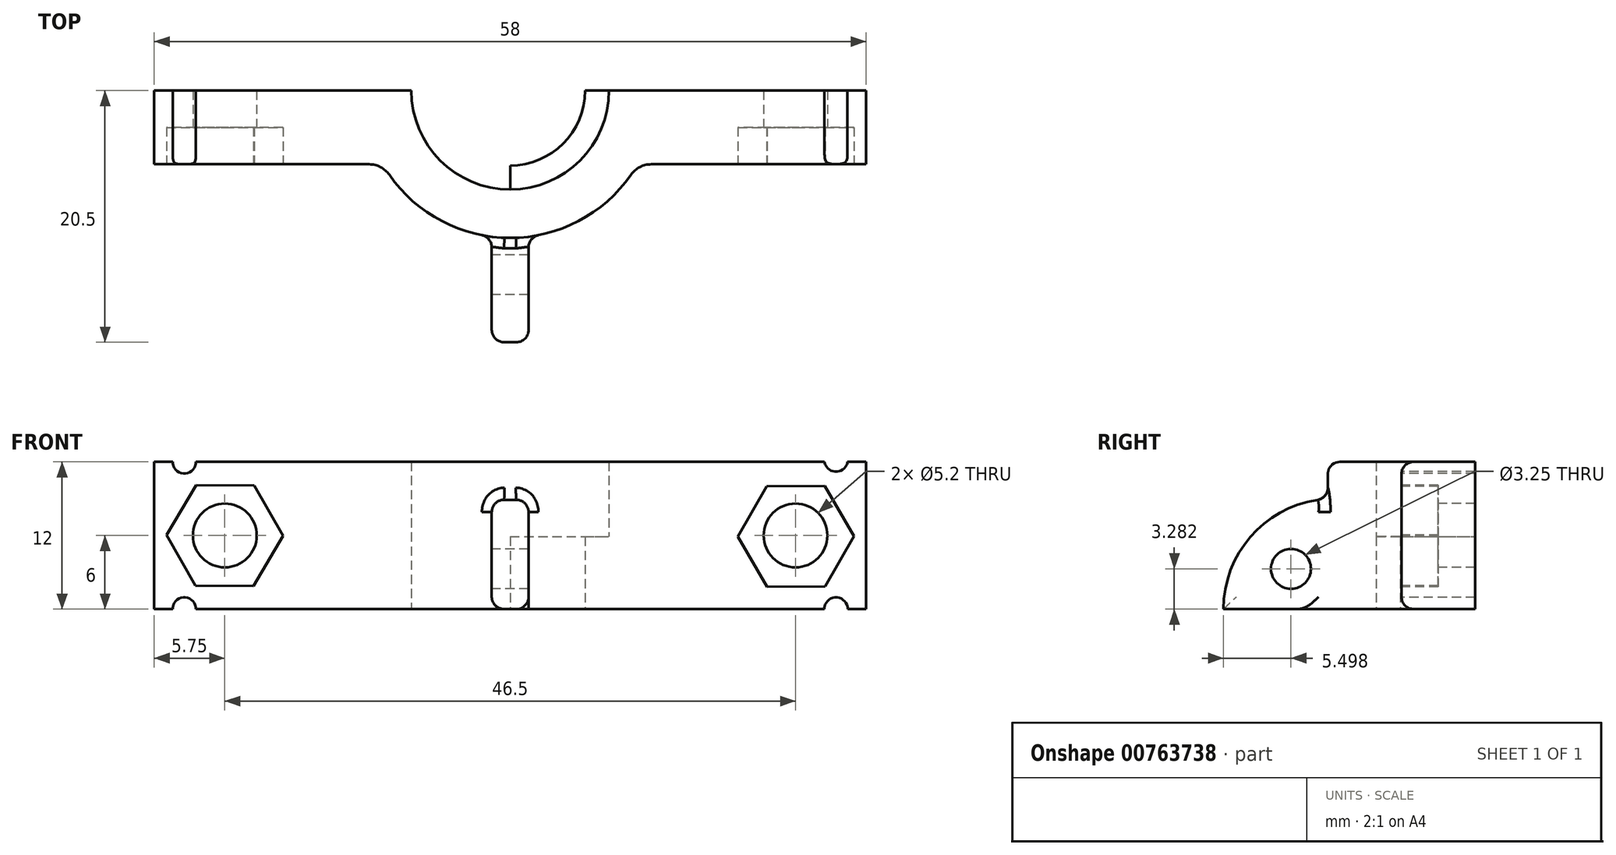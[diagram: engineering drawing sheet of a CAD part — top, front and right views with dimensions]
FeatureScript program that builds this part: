
annotation { "Feature Type Name" : "Feature", "Feature Type Description" : "" }
export const myFeature = defineFeature(function(context is Context, id is Id, definition is map)
    precondition{}
    {
        {
            var Q0;
            Q0=qCreatedBy(makeId("Top.planeOp"),FACE);
            var sketch = newSketch(context, id + "F0", { "sketchPlane" : qUnion([Q0])});
            skLineSegment(sketch, "E0", {"start": v(0, 28.15) * mm, "end": v(0, 0) * mm, "construction": true});
            skLineSegment(sketch, "E1.bottom", {"start": v(6.1, 0) * mm, "end": v(29, 0) * mm});
            skLineSegment(sketch, "E1.left", {"start": v(0, -6.1) * mm, "end": v(0, -12) * mm});
            skLineSegment(sketch, "E1.right", {"start": v(29, 0) * mm, "end": v(29, -6) * mm});
            skArc(sketch, "E2", {"start": v(0, -6.1) * mm, "mid": v(4.31, -4.31) * mm, "end": v(6.1, 0) * mm});
            skArc(sketch, "E3", {"start": v(0, -8.05) * mm, "mid": v(5.7, -5.7) * mm, "end": v(8.05, 0) * mm});
            skArc(sketch, "E4", {"start": v(0, -12) * mm, "mid": v(6, -10.4) * mm, "end": v(10.4, -6) * mm});
            skLineSegment(sketch, "E5", {"start": v(29, -6) * mm, "end": v(0, -6) * mm, "construction": true});
            skLineSegment(sketch, "E6", {"start": v(10.4, -6) * mm, "end": v(29, -6) * mm});
            skPoint(sketch, "E1.top.end.orphan", {"position": v(29, -12) * mm});
            skLineSegment(sketch, "E7", {"start": v(0, -12) * mm, "end": v(23.1, -12) * mm, "construction": true});
            skLineSegment(sketch, "E8.trimOffspring", {"start": v(0, -6.1) * mm, "end": v(0, -22.79) * mm, "construction": true});
            skLineSegment(sketch, "E9", {"start": v(0, 0) * mm, "end": v(0, -6.1) * mm, "construction": true});
            skLineSegment(sketch, "E10.MirrorCS", {"start": v(-10.4, -6) * mm, "end": v(-29, -6) * mm});
            skArc(sketch, "E11.MirrorCS", {"start": v(0, -6.1) * mm, "mid": v(-4.31, -4.31) * mm, "end": v(-6.1, 0) * mm});
            skArc(sketch, "E12.MirrorCS", {"start": v(0, -8.05) * mm, "mid": v(-5.7, -5.7) * mm, "end": v(-8.05, 0) * mm});
            skArc(sketch, "E13.MirrorCS", {"start": v(0, -12) * mm, "mid": v(-6, -10.4) * mm, "end": v(-10.4, -6) * mm});
            skLineSegment(sketch, "E14.MirrorCS", {"start": v(-29, -6) * mm, "end": v(0, -6) * mm, "construction": true});
            skLineSegment(sketch, "E15.MirrorCS", {"start": v(-6.1, 0) * mm, "end": v(-29, 0) * mm});
            skLineSegment(sketch, "E16.MirrorCS", {"start": v(-29, 0) * mm, "end": v(-29, -6) * mm});
            skPoint(sketch, "E17.orphan", {"position": v(-12, 0) * mm});
            skPoint(sketch, "E18.orphan", {"position": v(12, 0) * mm});
            skSolve(sketch);
        }
        {
            var Q0;
            Q0=makeQuery(id+"F0.imprint","IMPRINT",FACE,{"disambiguationData":[TD([[makeQuery(id+"F0.imprint","IMPRINT",EDGE,{"derivedFrom":sQuery(id+"F0.wireOp",EDGE,"E10.MirrorCS")}),-1.0]])]});
            var Q1;
            {var subQ0=sQuery(id+"F0.wireOp",EDGE,"E1.right");Q1=makeQuery(id+"F0.imprint","IMPRINT",FACE,{"disambiguationData":[TD([[makeQuery(id+"F0.imprint","IMPRINT",EDGE,{"derivedFrom":subQ0}),-1.0]])]});}
            extrude(context, id + "F1", {"entities" : qUnion([Q0, Q1]), "depth" : 12 * mm, "offsetDistance" : 25 * mm});
        }
        {
            var Q0;
            {var subQ0=sQuery(id+"F0.wireOp",EDGE,"E11.MirrorCS");Q0=makeQuery(id+"F0.imprint","IMPRINT",FACE,{"disambiguationData":[TD([[makeQuery(id+"F0.imprint","IMPRINT",EDGE,{"derivedFrom":subQ0}),1.0]])]});}
            var Q1;
            {var subQ0=sQuery(id+"F0.wireOp",EDGE,"E2");Q1=makeQuery(id+"F0.imprint","IMPRINT",FACE,{"disambiguationData":[TD([[makeQuery(id+"F0.imprint","IMPRINT",EDGE,{"derivedFrom":subQ0}),-1.0]])]});}
            extrude(context, id + "F2", {"entities" : qUnion([Q0, Q1]), "operationType" : NewBodyOperationType.ADD, "depth" : 5.9 * mm, "offsetDistance" : 25 * mm});
        }
        {
            var Q0;
            Q0=makeQuery(id+"F1.opExtrude","SWEPT_FACE",FACE,{"disambiguationData":[OSD([sQuery(id+"F0.wireOp",EDGE,"E10.MirrorCS")])]});
            var sketch = newSketch(context, id + "F3", { "sketchPlane" : qUnion([Q0])});
            skLineSegment(sketch, "E19", {"start": v(-29, 6) * mm, "end": v(33.2, 6) * mm, "construction": true});
            skLineSegment(sketch, "E20", {"start": v(29.12, 12) * mm, "end": v(37.37, 12) * mm, "construction": true});
            skLineSegment(sketch, "E21", {"start": v(29.05, 0) * mm, "end": v(37.37, 0) * mm, "construction": true});
            skCircle(sketch, "E22", {"center": v(-23.25, 6) * mm, "radius": 2.6 * mm});
            skCircle(sketch, "E23", {"center": v(23.25, 6) * mm, "radius": 2.6 * mm});
            skSolve(sketch);
        }
        {
            var Q0;
            Q0=makeQuery(id+"F3.imprint","IMPRINT",FACE,{"disambiguationData":[TD([[makeQuery(id+"F3.imprint","IMPRINT",EDGE,{"derivedFrom":sQuery(id+"F3.wireOp",EDGE,"E23")}),1.0]])]});
            var Q1;
            Q1=makeQuery(id+"F3.imprint","IMPRINT",FACE,{"disambiguationData":[TD([[makeQuery(id+"F3.imprint","IMPRINT",EDGE,{"derivedFrom":sQuery(id+"F3.wireOp",EDGE,"E22")}),1.0]])]});
            extrude(context, id + "F4", {"entities" : qUnion([Q0, Q1]), "operationType" : NewBodyOperationType.REMOVE, "oppositeDirection" : true, "depth" : 15 * mm, "offsetDistance" : 25 * mm});
        }
        {
            var Q0;
            Q0=makeQuery(id+"F1.opExtrude","SWEPT_FACE",FACE,{"disambiguationData":[OSD([sQuery(id+"F0.wireOp",EDGE,"E10.MirrorCS")])]});
            var sketch = newSketch(context, id + "F5", { "sketchPlane" : qUnion([Q0])});
            skCircle(sketch, "E24.cCircle", {"center": v(-23.25, 6) * mm, "radius": 4.1 * mm, "construction": true});
            skLineSegment(sketch, "E24.0", {"start": v(-20.86, 10.08) * mm, "end": v(-18.52, 5.97) * mm});
            skLineSegment(sketch, "E24.1", {"start": v(-18.52, 5.97) * mm, "end": v(-20.9, 1.89) * mm});
            skLineSegment(sketch, "E24.2", {"start": v(-20.9, 1.89) * mm, "end": v(-25.64, 1.92) * mm});
            skLineSegment(sketch, "E24.3", {"start": v(-25.64, 1.92) * mm, "end": v(-27.98, 6.03) * mm});
            skLineSegment(sketch, "E24.4", {"start": v(-27.98, 6.03) * mm, "end": v(-25.6, 10.11) * mm});
            skLineSegment(sketch, "E24.5", {"start": v(-25.6, 10.11) * mm, "end": v(-20.86, 10.08) * mm});
            skPoint(sketch, "E24.0.midPoint", {"position": v(-19.69, 8.03) * mm});
            skCircle(sketch, "E25.cCircle", {"center": v(23.28, 5.93) * mm, "radius": 4.1 * mm, "construction": true});
            skLineSegment(sketch, "E25.0", {"start": v(18.55, 5.91) * mm, "end": v(20.9, 10.02) * mm});
            skLineSegment(sketch, "E25.1", {"start": v(20.9, 10.02) * mm, "end": v(25.63, 10.04) * mm});
            skLineSegment(sketch, "E25.2", {"start": v(25.63, 10.04) * mm, "end": v(28.02, 5.95) * mm});
            skLineSegment(sketch, "E25.3", {"start": v(28.02, 5.95) * mm, "end": v(25.67, 1.84) * mm});
            skLineSegment(sketch, "E25.4", {"start": v(25.67, 1.84) * mm, "end": v(20.93, 1.82) * mm});
            skLineSegment(sketch, "E25.5", {"start": v(20.93, 1.82) * mm, "end": v(18.55, 5.91) * mm});
            skPoint(sketch, "E25.0.midPoint", {"position": v(19.72, 7.97) * mm});
            skSolve(sketch);
        }
        {
            var Q0;
            Q0=makeQuery(id+"F5.imprint","IMPRINT",FACE,{"disambiguationData":[TD([[makeQuery(id+"F5.imprint","IMPRINT",EDGE,{"derivedFrom":sQuery(id+"F5.wireOp",EDGE,"E24.0")}),-1.0]])]});
            var Q1;
            Q1=makeQuery(id+"F5.imprint","IMPRINT",FACE,{"disambiguationData":[TD([[makeQuery(id+"F5.imprint","IMPRINT",EDGE,{"derivedFrom":sQuery(id+"F5.wireOp",EDGE,"E25.0")}),-1.0]])]});
            extrude(context, id + "F6", {"entities" : qUnion([Q0, Q1]), "operationType" : NewBodyOperationType.REMOVE, "oppositeDirection" : true, "depth" : 3 * mm, "offsetDistance" : 25 * mm});
        }
        {
            var Q0;
            Q0=makeQuery(id+"F1.opExtrude","SWEPT_FACE",FACE,{"disambiguationData":[OSD([sQuery(id+"F0.wireOp",EDGE,"E10.MirrorCS")])]});
            var sketch = newSketch(context, id + "F7", { "sketchPlane" : qUnion([Q0])});
            skCircle(sketch, "E26", {"center": v(-26.55, 12) * mm, "radius": 0.95 * mm});
            skLineSegment(sketch, "E27", {"start": v(-33.66, 6) * mm, "end": v(33.7, 6) * mm, "construction": true});
            skPoint(sketch, "E27.startSnap0", {"position": v(-29, 6) * mm});
            skLineSegment(sketch, "E28", {"start": v(0, -5.22) * mm, "end": v(0, 20.12) * mm, "construction": true});
            skCircle(sketch, "E29", {"center": v(-26.55, 0) * mm, "radius": 0.95 * mm});
            skCircle(sketch, "E30", {"center": v(26.55, 12.15) * mm, "radius": 0.95 * mm});
            skCircle(sketch, "E31", {"center": v(26.55, 0) * mm, "radius": 0.95 * mm});
            skSolve(sketch);
        }
        {
            var Q0;
            {var subQ0=sQuery(id+"F7.wireOp",EDGE,"E26");var subQ1=makeQuery(id+"F1.opExtrude","CAP_EDGE",EDGE,{"disambiguationData":[OSD([sQuery(id+"F0.wireOp",EDGE,"E10.MirrorCS")])],"isStart":false});var subQ2=makeQuery(id+"F7.imprint","INTERSECT",VERTEX,{"disambiguationData":[OD(0.0)],"derivedFrom":[subQ1,subQ0]});Q0=makeQuery(id+"F7.imprint","IMPRINT",FACE,{"disambiguationData":[TD([[makeQuery(id+"F7.imprint","IMPRINT",EDGE,{"disambiguationData":[TD([[subQ2,1.0]])],"derivedFrom":subQ0}),1.0]])]});}
            var Q1;
            {var subQ0=sQuery(id+"F7.wireOp",EDGE,"E29");var subQ1=makeQuery(id+"F1.opExtrude","CAP_EDGE",EDGE,{"disambiguationData":[OSD([sQuery(id+"F0.wireOp",EDGE,"E10.MirrorCS")])],"isStart":true});var subQ2=makeQuery(id+"F7.imprint","INTERSECT",VERTEX,{"disambiguationData":[OD(0.0)],"derivedFrom":[subQ1,subQ0]});Q1=makeQuery(id+"F7.imprint","IMPRINT",FACE,{"disambiguationData":[TD([[makeQuery(id+"F7.imprint","IMPRINT",EDGE,{"disambiguationData":[TD([[subQ2,-1.0]])],"derivedFrom":subQ0}),1.0]])]});}
            var Q2;
            Q2=makeQuery(id+"F7.imprint","IMPRINT",FACE,{"disambiguationData":[TD([[makeQuery(id+"F7.imprint","IMPRINT",EDGE,{"derivedFrom":sQuery(id+"F7.wireOp",EDGE,"E30")}),1.0]])]});
            var Q3;
            Q3=makeQuery(id+"F7.imprint","IMPRINT",FACE,{"disambiguationData":[TD([[makeQuery(id+"F7.imprint","IMPRINT",EDGE,{"derivedFrom":sQuery(id+"F7.wireOp",EDGE,"E31")}),1.0]])]});
            extrude(context, id + "F8", {"entities" : qUnion([Q0, Q1, Q2, Q3]), "operationType" : NewBodyOperationType.REMOVE, "oppositeDirection" : true, "depth" : 25 * mm, "offsetDistance" : 25 * mm});
        }
        {
            var Q0;
            Q0=makeQuery(id+"F1.opExtrude","SWEPT_EDGE",EDGE,{"disambiguationData":[OSD([sQuery(id+"F0.wireOp",EDGE,"E4"),sQuery(id+"F0.wireOp",EDGE,"E6")])]});
            var Q1;
            Q1=makeQuery(id+"F1.opExtrude","SWEPT_EDGE",EDGE,{"disambiguationData":[OSD([sQuery(id+"F0.wireOp",EDGE,"E10.MirrorCS"),sQuery(id+"F0.wireOp",EDGE,"E13.MirrorCS")])]});
            fillet(context, id + "F9", {"entities" : qUnion([Q0, Q1]), "radius" : 2 * mm, "tangentPropagation" : true, "allowEdgeOverflow" : false});
        }
        {
            var Q0;
            Q0=qCreatedBy(makeId("Front.planeOp"),FACE);
            cPlane(context, id + "F10", {"entities" : qUnion([Q0]), "cplaneType" : CPlaneType.OFFSET, "offset" : 11.5 * mm, "width" : 150 * mm, "height" : 150 * mm});
        }
        {
            var Q0;
            Q0=qCreatedBy(id+"F10.planeOp",FACE);
            var sketch = newSketch(context, id + "F11", { "sketchPlane" : qUnion([Q0])});
            skLineSegment(sketch, "E32", {"start": v(0, -11.38) * mm, "end": v(0, 44.34) * mm, "construction": true});
            skLineSegment(sketch, "E33", {"start": v(-34.64, 0) * mm, "end": v(49.3, 0) * mm, "construction": true});
            skLineSegment(sketch, "E34", {"start": v(-29.79, 5.73) * mm, "end": v(39.82, 5.73) * mm, "construction": true});
            skLineSegment(sketch, "E35", {"start": v(-29.29, 9) * mm, "end": v(32.48, 9) * mm, "construction": true});
            skLineSegment(sketch, "E36.bottom", {"start": v(-1.5, 9) * mm, "end": v(1.5, 9) * mm});
            skLineSegment(sketch, "E36.top", {"start": v(-1.5, 0) * mm, "end": v(1.5, 0) * mm});
            skLineSegment(sketch, "E36.left", {"start": v(-1.5, 9) * mm, "end": v(-1.5, 0) * mm});
            skLineSegment(sketch, "E36.right", {"start": v(1.5, 9) * mm, "end": v(1.5, 0) * mm});
            skSolve(sketch);
        }
        {
            var Q0;
            Q0=makeQuery(id+"F11.imprint","IMPRINT",FACE,{"disambiguationData":[TD([[makeQuery(id+"F11.imprint","IMPRINT",EDGE,{"derivedFrom":sQuery(id+"F11.wireOp",EDGE,"E36.bottom")}),-1.0]])]});
            var Q1;
            Q1=sQuery(id+"F11.wireOp",EDGE,"E36.top");
            revolve(context, id + "F12", {"operationType" : NewBodyOperationType.ADD, "surfaceOperationType" : NewSurfaceOperationType.NEW, "entities" : qUnion([Q0]), "axis" : qUnion([Q1]), "revolveType" : RevolveType.ONE_DIRECTION, "angle" : 90 * degree});
        }
        {
            var Q0;
            Q0=makeQuery(id+"F12.opRevolve","SWEPT_FACE",FACE,{"disambiguationData":[OSD([sQuery(id+"F11.wireOp",EDGE,"E36.left")])]});
            var Q1;
            Q1=makeQuery(id+"F1.opExtrude","SWEPT_FACE",FACE,{"disambiguationData":[OSD([sQuery(id+"F0.wireOp",EDGE,"E4"),sQuery(id+"F0.wireOp",EDGE,"E13.MirrorCS")])]});
            var Q2;
            Q2=makeQuery(id+"F12.boolean.opBoolean","INTERSECT",EDGE,{"derivedFrom":[makeQuery(id+"F1.opExtrude","SWEPT_FACE",FACE,{"disambiguationData":[OSD([sQuery(id+"F0.wireOp",EDGE,"E4"),sQuery(id+"F0.wireOp",EDGE,"E13.MirrorCS")])]}),makeQuery(id+"F12.opRevolve","SWEPT_FACE",FACE,{"disambiguationData":[OSD([sQuery(id+"F11.wireOp",EDGE,"E36.bottom")])]})]});
            var Q3;
            Q3=makeQuery(id+"F12.boolean.opBoolean","INTERSECT",EDGE,{"derivedFrom":[makeQuery(id+"F1.opExtrude","SWEPT_FACE",FACE,{"disambiguationData":[OSD([sQuery(id+"F0.wireOp",EDGE,"E4"),sQuery(id+"F0.wireOp",EDGE,"E13.MirrorCS")])]}),makeQuery(id+"F12.opRevolve","SWEPT_FACE",FACE,{"disambiguationData":[OSD([sQuery(id+"F11.wireOp",EDGE,"E36.right")])]})]});
            var Q4;
            Q4=makeQuery(id+"F12.opRevolve","SWEPT_EDGE",EDGE,{"disambiguationData":[OSD([sQuery(id+"F11.wireOp",EDGE,"E36.bottom"),sQuery(id+"F11.wireOp",EDGE,"E36.right")])]});
            fillet(context, id + "F13", {"entities" : qUnion([Q0, Q1, Q2, Q3, Q4]), "radius" : 1 * mm, "tangentPropagation" : true, "allowEdgeOverflow" : false});
        }
        {
            var Q0;
            Q0=makeQuery(id+"F12.opRevolve","SWEPT_FACE",FACE,{"disambiguationData":[OSD([sQuery(id+"F11.wireOp",EDGE,"E36.left")])]});
            var sketch = newSketch(context, id + "F14", { "sketchPlane" : qUnion([Q0])});
            skPoint(sketch, "E37", {"position": v(17.25, 5.56) * mm});
            skLineSegment(sketch, "E38", {"start": v(12.76, 1) * mm, "end": v(17.25, 5.56) * mm, "construction": true});
            skPoint(sketch, "E39", {"position": v(15, 3.28) * mm});
            skCircle(sketch, "E40", {"center": v(15, 3.28) * mm, "radius": 1.63 * mm});
            skSolve(sketch);
        }
        {
            var Q0;
            Q0=makeQuery(id+"F14.imprint","IMPRINT",FACE,{"disambiguationData":[TD([[makeQuery(id+"F14.imprint","IMPRINT",EDGE,{"derivedFrom":sQuery(id+"F14.wireOp",EDGE,"E40")}),1.0]])]});
            extrude(context, id + "F15", {"entities" : qUnion([Q0]), "operationType" : NewBodyOperationType.REMOVE, "oppositeDirection" : true, "depth" : 5 * mm, "offsetDistance" : 25 * mm});
        }
    });
